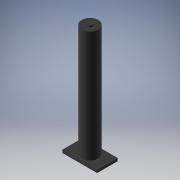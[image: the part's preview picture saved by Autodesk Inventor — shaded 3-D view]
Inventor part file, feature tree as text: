
AUTODESK INVENTOR PART (.ipt)
format: ipt  version: 2018 (Build 220112000, 112)  size: 113,152 bytes
history: native  units: in
note: dims shown in document units (in); Inventor stores cm internally (conversion verified against a paired STEP export)
features: extrude x4, sketch x4
ambient origin geometry x8: Origin, YZ Plane, XZ Plane, XY Plane, X Axis, Y Axis, Z Axis, Center Point
bodies: Solid1 (feature_tree)
feature tree (8):
  extrude  "Extrusion1"  Depth=2.8976in TaperAngle=0.0deg
  extrude  "Extrusion2"  Depth=2.7874in TaperAngle=0.0deg
  extrude  "Extrusion3"  Depth=0.0394in
  extrude  "Extrusion4"  Depth=0.5295in
  sketch  "Sketch1"  dims[d0=0.4252in d1=2.8976in d2=0.0in]
  sketch  "Sketch2"  dims[d3=0.252in d4=2.7874in d5=0.0in]
  sketch  "Sketch3"  dims[d6=0.0394in d7=0.0in d8=0.2648in]
  sketch  "Sketch4"  dims[d9=0.5295in d10=0.4498in d11=0.8996in d12=0.0689in d13=0.0in d17=0.5295in]
